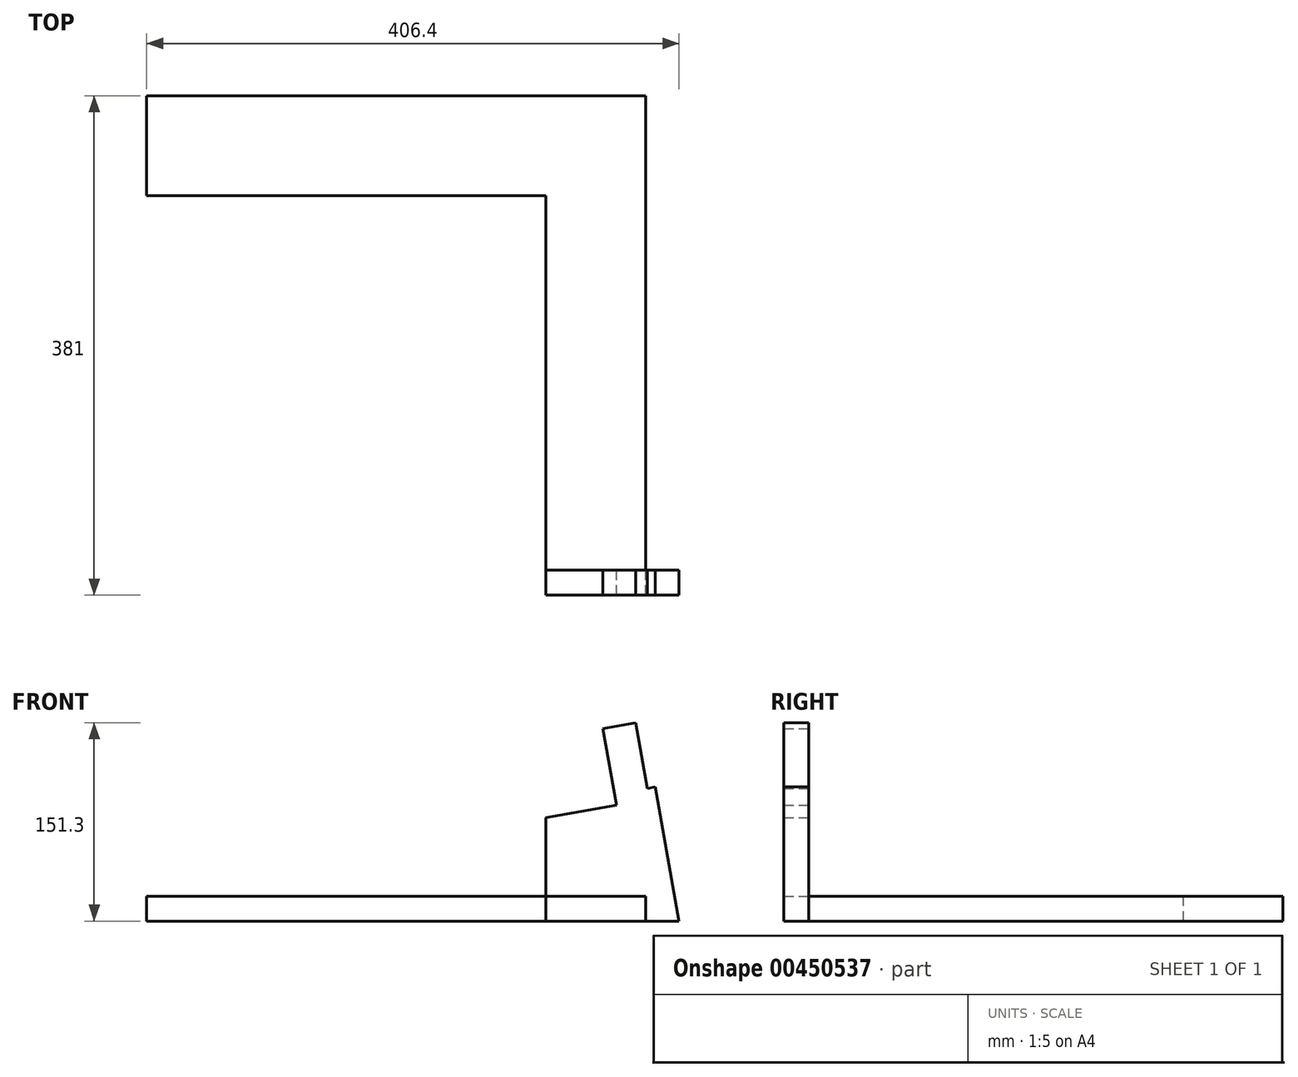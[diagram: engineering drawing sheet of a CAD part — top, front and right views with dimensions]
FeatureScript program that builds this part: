
annotation { "Feature Type Name" : "Feature", "Feature Type Description" : "" }
export const myFeature = defineFeature(function(context is Context, id is Id, definition is map)
    precondition{}
    {
        {
            var Q0;
            Q0=qCreatedBy(makeId("Front.planeOp"),FACE);
            var sketch = newSketch(context, id + "F0", { "sketchPlane" : qUnion([Q0])});
            skLineSegment(sketch, "E0", {"start": v(0, 0) * mm, "end": v(-25.4, 0) * mm});
            skLineSegment(sketch, "E1", {"start": v(-101.6, 19.05) * mm, "end": v(-101.6, 78.95) * mm});
            skLineSegment(sketch, "E2", {"start": v(0, 0) * mm, "end": v(-18.05, 102.37) * mm});
            skLineSegment(sketch, "E3", {"start": v(-33.13, 151.3) * mm, "end": v(-24.3, 101.27) * mm});
            skLineSegment(sketch, "E4", {"start": v(-24.3, 101.27) * mm, "end": v(-18.05, 102.37) * mm});
            skLineSegment(sketch, "E5", {"start": v(-33.13, 151.3) * mm, "end": v(-58.14, 146.89) * mm});
            skLineSegment(sketch, "E6", {"start": v(-58.14, 146.89) * mm, "end": v(-47.83, 88.43) * mm});
            skLineSegment(sketch, "E7", {"start": v(-47.83, 88.43) * mm, "end": v(-101.6, 78.95) * mm});
            skLineSegment(sketch, "E8.top", {"start": v(-101.6, 19.05) * mm, "end": v(-25.4, 19.05) * mm});
            skLineSegment(sketch, "E8.right", {"start": v(-25.4, 0) * mm, "end": v(-25.4, 19.05) * mm});
            skSolve(sketch);
        }
        {
            var Q0;
            Q0=makeQuery(id+"F0.imprint","IMPRINT",FACE,{"disambiguationData":[TD([[makeQuery(id+"F0.imprint","IMPRINT",EDGE,{"derivedFrom":sQuery(id+"F0.wireOp",EDGE,"E0")}),-1.0]])]});
            extrude(context, id + "F1", {"entities" : qUnion([Q0]), "depth" : 19.05 * mm});
        }
        {
            var Q0;
            Q0=qCreatedBy(makeId("Top.planeOp"),FACE);
            var sketch = newSketch(context, id + "F2", { "sketchPlane" : qUnion([Q0])});
            skPoint(sketch, "E9.0", {"position": v(-25.4, -19.05) * mm});
            skLineSegment(sketch, "E10.bottom", {"start": v(-25.4, -19.05) * mm, "end": v(-101.6, -19.05) * mm});
            skLineSegment(sketch, "E10.left", {"start": v(-25.4, -19.05) * mm, "end": v(-25.4, 285.75) * mm});
            skLineSegment(sketch, "E10.right", {"start": v(-101.6, -19.05) * mm, "end": v(-101.6, 285.75) * mm});
            skLineSegment(sketch, "E11.bottom", {"start": v(-101.6, 285.75) * mm, "end": v(-406.4, 285.75) * mm});
            skLineSegment(sketch, "E11.top", {"start": v(-25.4, 361.95) * mm, "end": v(-406.4, 361.95) * mm});
            skLineSegment(sketch, "E11.left", {"start": v(-25.4, 285.75) * mm, "end": v(-25.4, 361.95) * mm});
            skLineSegment(sketch, "E11.right", {"start": v(-406.4, 285.75) * mm, "end": v(-406.4, 361.95) * mm});
            skSolve(sketch);
        }
        {
            var Q0;
            Q0=makeQuery(id+"F2.imprint","IMPRINT",FACE,{"disambiguationData":[TD([[makeQuery(id+"F2.imprint","IMPRINT",EDGE,{"derivedFrom":sQuery(id+"F2.wireOp",EDGE,"E10.bottom")}),-1.0]])]});
            extrude(context, id + "F3", {"entities" : qUnion([Q0]), "depth" : 19.05 * mm});
        }
    });
